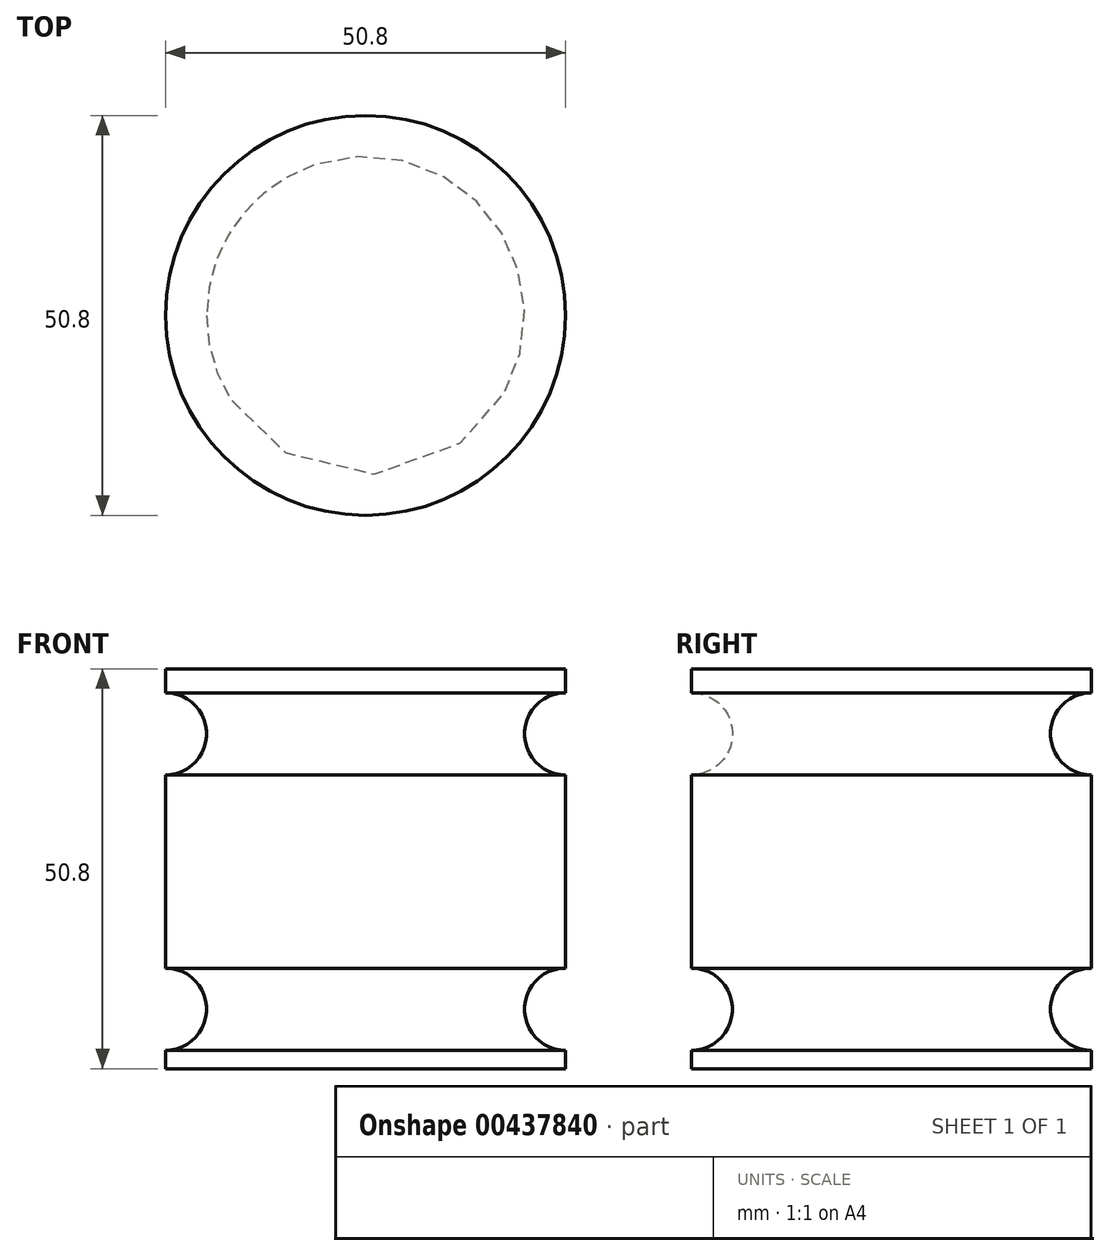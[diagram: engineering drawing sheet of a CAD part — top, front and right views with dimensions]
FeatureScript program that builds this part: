
annotation { "Feature Type Name" : "Feature", "Feature Type Description" : "" }
export const myFeature = defineFeature(function(context is Context, id is Id, definition is map)
    precondition{}
    {
        {
            var Q0;
            Q0=qCreatedBy(makeId("Front.planeOp"),FACE);
            var sketch = newSketch(context, id + "F0", { "sketchPlane" : qUnion([Q0])});
            skLineSegment(sketch, "E0.bottom", {"start": v(0, 0) * mm, "end": v(-25.4, 0) * mm});
            skLineSegment(sketch, "E0.top", {"start": v(0, 50.8) * mm, "end": v(-25.4, 50.8) * mm});
            skLineSegment(sketch, "E0.left", {"start": v(0, 0) * mm, "end": v(0, 2.35) * mm});
            skLineSegment(sketch, "E0.right", {"start": v(-25.4, 0) * mm, "end": v(-25.4, 50.8) * mm});
            skArc(sketch, "E1", {"start": v(0, 47.75) * mm, "mid": v(-5.2, 42.54) * mm, "end": v(0, 37.34) * mm});
            skArc(sketch, "E2", {"start": v(0, 12.77) * mm, "mid": v(-5.2, 7.56) * mm, "end": v(0, 2.35) * mm});
            skLineSegment(sketch, "E3.trimOffspring", {"start": v(0, 12.77) * mm, "end": v(0, 37.34) * mm});
            skLineSegment(sketch, "E4.trimOffspring", {"start": v(0, 47.75) * mm, "end": v(0, 50.8) * mm});
            skSolve(sketch);
        }
        {
            var Q0;
            Q0 = qSketchRegion(id + "F0", true);
            var Q1;
            Q1=sQuery(id+"F0.wireOp",EDGE,"E0.right");
            revolve(context, id + "F1", {"entities" : qUnion([Q0]), "axis" : qUnion([Q1]), "revolveType" : RevolveType.FULL});
        }
    });
